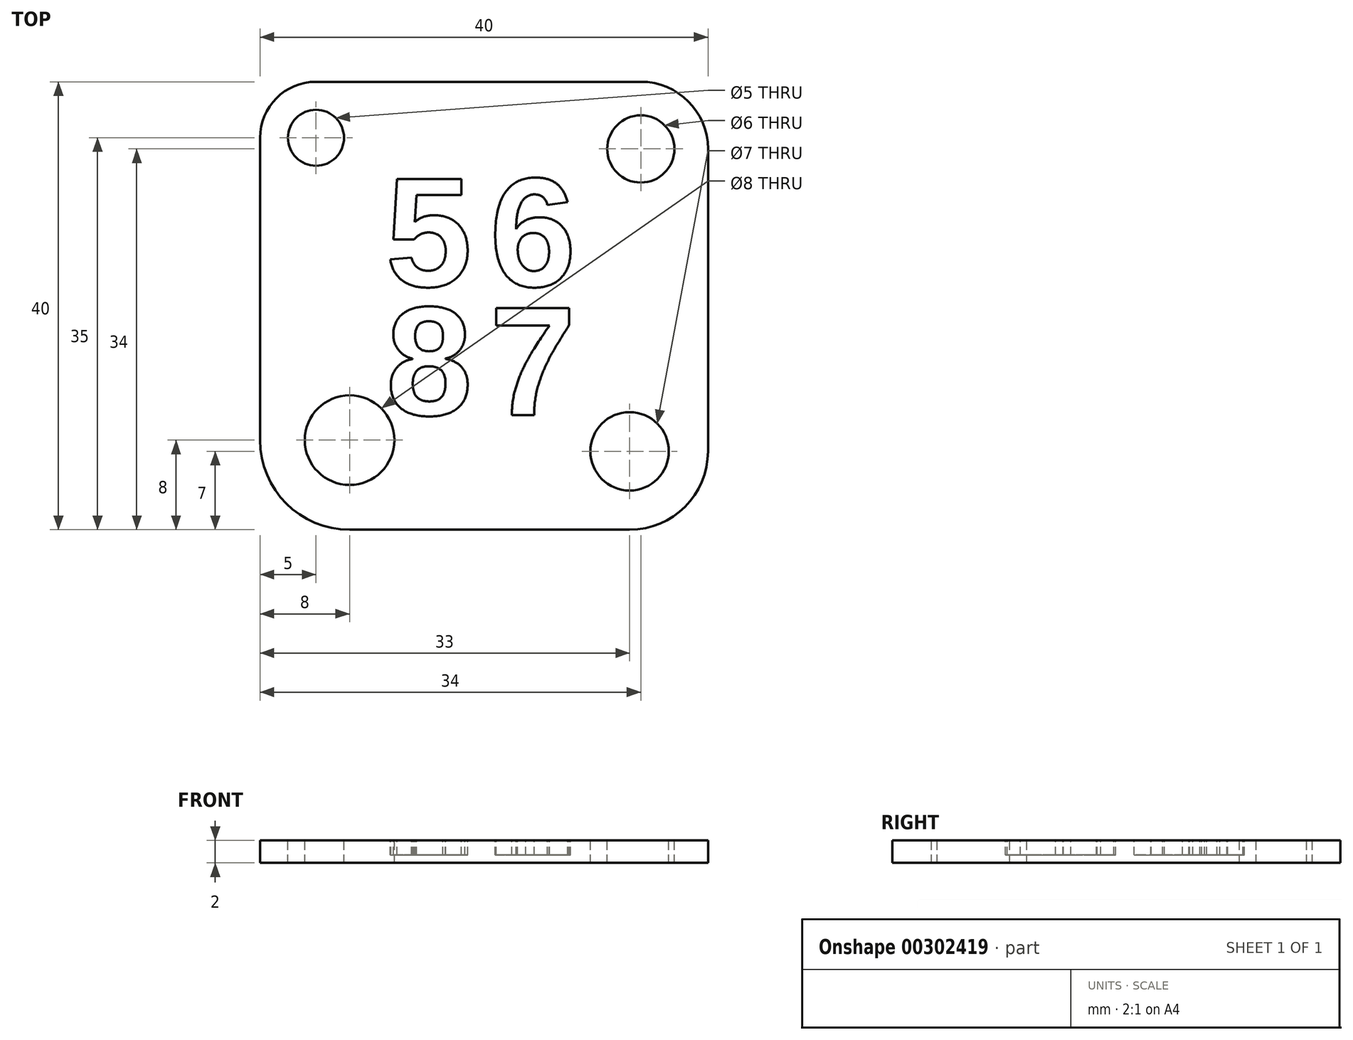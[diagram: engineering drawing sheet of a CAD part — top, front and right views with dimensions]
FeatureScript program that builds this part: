
annotation { "Feature Type Name" : "Feature", "Feature Type Description" : "" }
export const myFeature = defineFeature(function(context is Context, id is Id, definition is map)
    precondition{}
    {
        {
            var Q0;
            Q0=qCreatedBy(makeId("Top.planeOp"),FACE);
            var sketch = newSketch(context, id + "F0", { "sketchPlane" : qUnion([Q0])});
            skLineSegment(sketch, "E0.bottom", {"start": v(-15, 20) * mm, "end": v(14, 20) * mm});
            skLineSegment(sketch, "E0.top", {"start": v(-12, -20) * mm, "end": v(13, -20) * mm});
            skLineSegment(sketch, "E0.left", {"start": v(-20, 15) * mm, "end": v(-20, -12) * mm});
            skLineSegment(sketch, "E0.right", {"start": v(20, 14) * mm, "end": v(20, -13) * mm});
            skPoint(sketch, "E0.middle", {"position": v(0, 0) * mm});
            skPoint(sketch, "E1.visualSharp", {"position": v(-20, 20) * mm});
            skArc(sketch, "E1.filletArc", {"start": v(-15, 20) * mm, "mid": v(-18.54, 18.54) * mm, "end": v(-20, 15) * mm});
            skPoint(sketch, "E2.visualSharp", {"position": v(20, 20) * mm});
            skArc(sketch, "E2.filletArc", {"start": v(20, 14) * mm, "mid": v(18.24, 18.24) * mm, "end": v(14, 20) * mm});
            skPoint(sketch, "E3.visualSharp", {"position": v(20, -20) * mm});
            skArc(sketch, "E3.filletArc", {"start": v(13, -20) * mm, "mid": v(17.95, -17.95) * mm, "end": v(20, -13) * mm});
            skPoint(sketch, "E4.visualSharp", {"position": v(-20, -20) * mm});
            skArc(sketch, "E4.filletArc", {"start": v(-20, -12) * mm, "mid": v(-17.66, -17.66) * mm, "end": v(-12, -20) * mm});
            skSolve(sketch);
        }
        {
            var Q0;
            Q0=makeQuery(id+"F0.imprint","IMPRINT",FACE,{"disambiguationData":[TD([[makeQuery(id+"F0.imprint","IMPRINT",EDGE,{"derivedFrom":sQuery(id+"F0.wireOp",EDGE,"E0.bottom")}),-1.0]])]});
            extrude(context, id + "F1", {"entities" : qUnion([Q0]), "depth" : 2 * mm});
        }
        {
            var Q0;
            Q0=makeQuery(id+"F1.opExtrude","CAP_FACE",FACE,{"disambiguationData":[OSD([sQuery(id+"F0.wireOp",EDGE,"E0.bottom"),sQuery(id+"F0.wireOp",EDGE,"E0.top"),sQuery(id+"F0.wireOp",EDGE,"E0.left"),sQuery(id+"F0.wireOp",EDGE,"E0.right"),sQuery(id+"F0.wireOp",EDGE,"E1.filletArc"),sQuery(id+"F0.wireOp",EDGE,"E2.filletArc"),sQuery(id+"F0.wireOp",EDGE,"E3.filletArc"),sQuery(id+"F0.wireOp",EDGE,"E4.filletArc")])],"isStart":false});
            var sketch = newSketch(context, id + "F2", { "sketchPlane" : qUnion([Q0])});
            skLineSegment(sketch, "E5.bottom", {"start": v(-0.5, 0.25) * mm, "end": v(0.5, 0.25) * mm});
            skLineSegment(sketch, "E5.top", {"start": v(-0.5, 1.75) * mm, "end": v(0.5, 1.75) * mm});
            skLineSegment(sketch, "E5.left", {"start": v(-0.5, 0.25) * mm, "end": v(-0.5, 1.75) * mm});
            skLineSegment(sketch, "E5.right", {"start": v(0.5, 0.25) * mm, "end": v(0.5, 1.75) * mm});
            skPoint(sketch, "E5.middle", {"position": v(0, 1) * mm});
            skPoint(sketch, "E6", {"position": v(-0.5, 1.75) * mm});
            skText(sketch, "E7", { "text": "5", "fontName": "Arimo-Bold.ttf"});
            skText(sketch, "E8", { "text": "6", "fontName": "Arimo-Bold.ttf"});
            skText(sketch, "E9", { "text": "8", "fontName": "Arimo-Bold.ttf"});
            skText(sketch, "E10", { "text": "7", "fontName": "Arimo-Bold.ttf"});
            skCircle(sketch, "E11", {"center": v(-12, -12) * mm, "radius": 4 * mm});
            skCircle(sketch, "E12", {"center": v(-15, 15) * mm, "radius": 2.5 * mm});
            skCircle(sketch, "E13", {"center": v(14, 14) * mm, "radius": 3 * mm});
            skCircle(sketch, "E14", {"center": v(13, -13) * mm, "radius": 3.5 * mm});
            const initialGuessF2  = {"E7": [-0.0088, 0.00175, 1, 0, 0.01], "E8": [0.0005, 0.00175, 1, 0, 0.01], "E9": [-0.00876, -0.00975, 1, 0, 0.01], "E10": [0.0005, -0.00975, 1, 0, 0.01]};
            skSetInitialGuess(sketch, initialGuessF2);
            skSolve(sketch);
        }
        {
            var Q0;
            Q0=makeQuery(id+"F2.imprint","IMPRINT",FACE,{"disambiguationData":[TD([[makeQuery(id+"F2.imprint","IMPRINT",EDGE,{"derivedFrom":sQuery(id+"F2.wireOp",EDGE,"E7.sketch_text.stroke-0")}),-1.0]])]});
            var Q1;
            Q1=makeQuery(id+"F2.imprint","IMPRINT",FACE,{"disambiguationData":[TD([[makeQuery(id+"F2.imprint","IMPRINT",EDGE,{"derivedFrom":sQuery(id+"F2.wireOp",EDGE,"E8.sketch_text.stroke-0")}),-1.0]])]});
            var Q2;
            Q2=makeQuery(id+"F2.imprint","IMPRINT",FACE,{"disambiguationData":[TD([[makeQuery(id+"F2.imprint","IMPRINT",EDGE,{"derivedFrom":sQuery(id+"F2.wireOp",EDGE,"E10.sketch_text.stroke-0")}),-1.0]])]});
            var Q3;
            Q3=makeQuery(id+"F2.imprint","IMPRINT",FACE,{"disambiguationData":[TD([[makeQuery(id+"F2.imprint","IMPRINT",EDGE,{"derivedFrom":sQuery(id+"F2.wireOp",EDGE,"E9.sketch_text.stroke-0")}),-1.0]])]});
            extrude(context, id + "F3", {"entities" : qUnion([Q0, Q1, Q2, Q3]), "operationType" : NewBodyOperationType.REMOVE, "oppositeDirection" : true, "depth" : 1.3 * mm});
        }
        {
            var Q0;
            Q0=makeQuery(id+"F2.imprint","IMPRINT",FACE,{"disambiguationData":[TD([[makeQuery(id+"F2.imprint","IMPRINT",EDGE,{"derivedFrom":sQuery(id+"F2.wireOp",EDGE,"E12")}),1.0]])]});
            var Q1;
            Q1=makeQuery(id+"F2.imprint","IMPRINT",FACE,{"disambiguationData":[TD([[makeQuery(id+"F2.imprint","IMPRINT",EDGE,{"derivedFrom":sQuery(id+"F2.wireOp",EDGE,"E13")}),1.0]])]});
            var Q2;
            Q2=makeQuery(id+"F2.imprint","IMPRINT",FACE,{"disambiguationData":[TD([[makeQuery(id+"F2.imprint","IMPRINT",EDGE,{"derivedFrom":sQuery(id+"F2.wireOp",EDGE,"E14")}),1.0]])]});
            var Q3;
            Q3=makeQuery(id+"F2.imprint","IMPRINT",FACE,{"disambiguationData":[TD([[makeQuery(id+"F2.imprint","IMPRINT",EDGE,{"derivedFrom":sQuery(id+"F2.wireOp",EDGE,"E11")}),1.0]])]});
            var Q4;
            Q4=sQuery(id+"F2.wireOp",EDGE,"E12");
            var Q5;
            Q5=sQuery(id+"F2.wireOp",EDGE,"E13");
            var Q6;
            Q6=sQuery(id+"F2.wireOp",EDGE,"E14");
            var Q7;
            Q7=sQuery(id+"F2.wireOp",EDGE,"E11");
            extrude(context, id + "F4", {"entities" : qUnion([Q0, Q1, Q2, Q3]), "operationType" : NewBodyOperationType.REMOVE, "surfaceEntities" : qUnion([Q4, Q5, Q6, Q7]), "oppositeDirection" : true, "depth" : 25 * mm});
        }
    });
